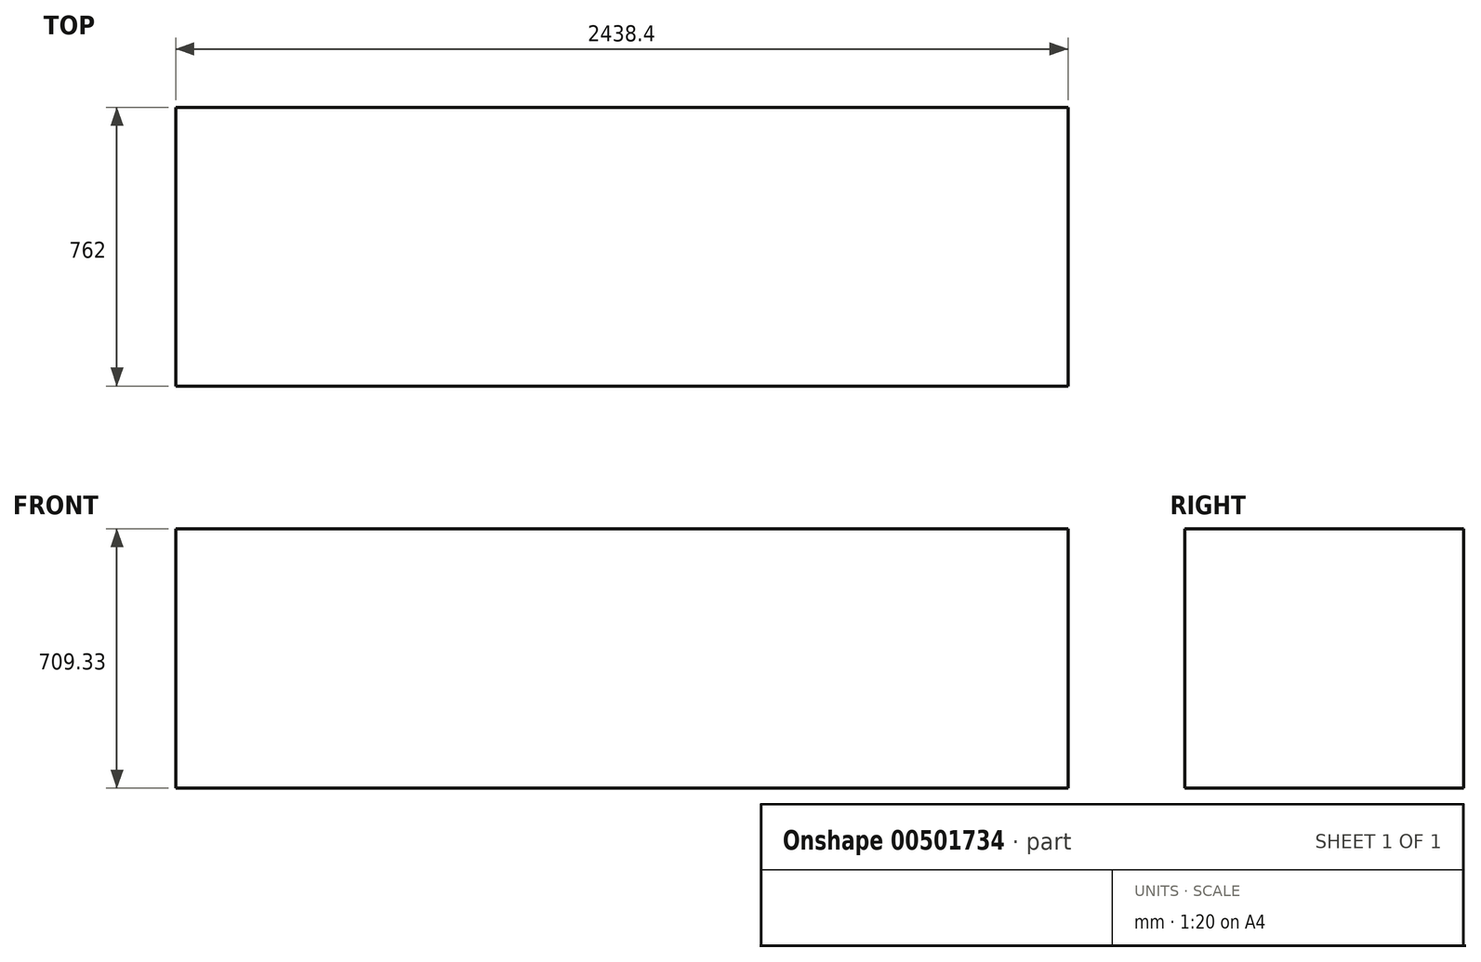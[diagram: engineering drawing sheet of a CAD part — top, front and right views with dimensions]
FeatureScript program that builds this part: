
annotation { "Feature Type Name" : "Feature", "Feature Type Description" : "" }
export const myFeature = defineFeature(function(context is Context, id is Id, definition is map)
    precondition{}
    {
        {
            var Q0;
            Q0=qCreatedBy(makeId("Top.planeOp"),FACE);
            var sketch = newSketch(context, id + "F0", { "sketchPlane" : qUnion([Q0])});
            skLineSegment(sketch, "E0.bottom", {"start": v(-1256.05, 0) * mm, "end": v(1182.35, 0) * mm});
            skLineSegment(sketch, "E0.top", {"start": v(-1256.05, 762) * mm, "end": v(1182.35, 762) * mm});
            skLineSegment(sketch, "E0.left", {"start": v(-1256.05, 0) * mm, "end": v(-1256.05, 762) * mm});
            skLineSegment(sketch, "E0.right", {"start": v(1182.35, 0) * mm, "end": v(1182.35, 762) * mm});
            skSolve(sketch);
        }
        {
            var Q0;
            Q0 = qSketchRegion(id + "F0", true);
            extrude(context, id + "F1", {"entities" : qUnion([Q0]), "depth" : 709.33 * mm});
        }
    });
